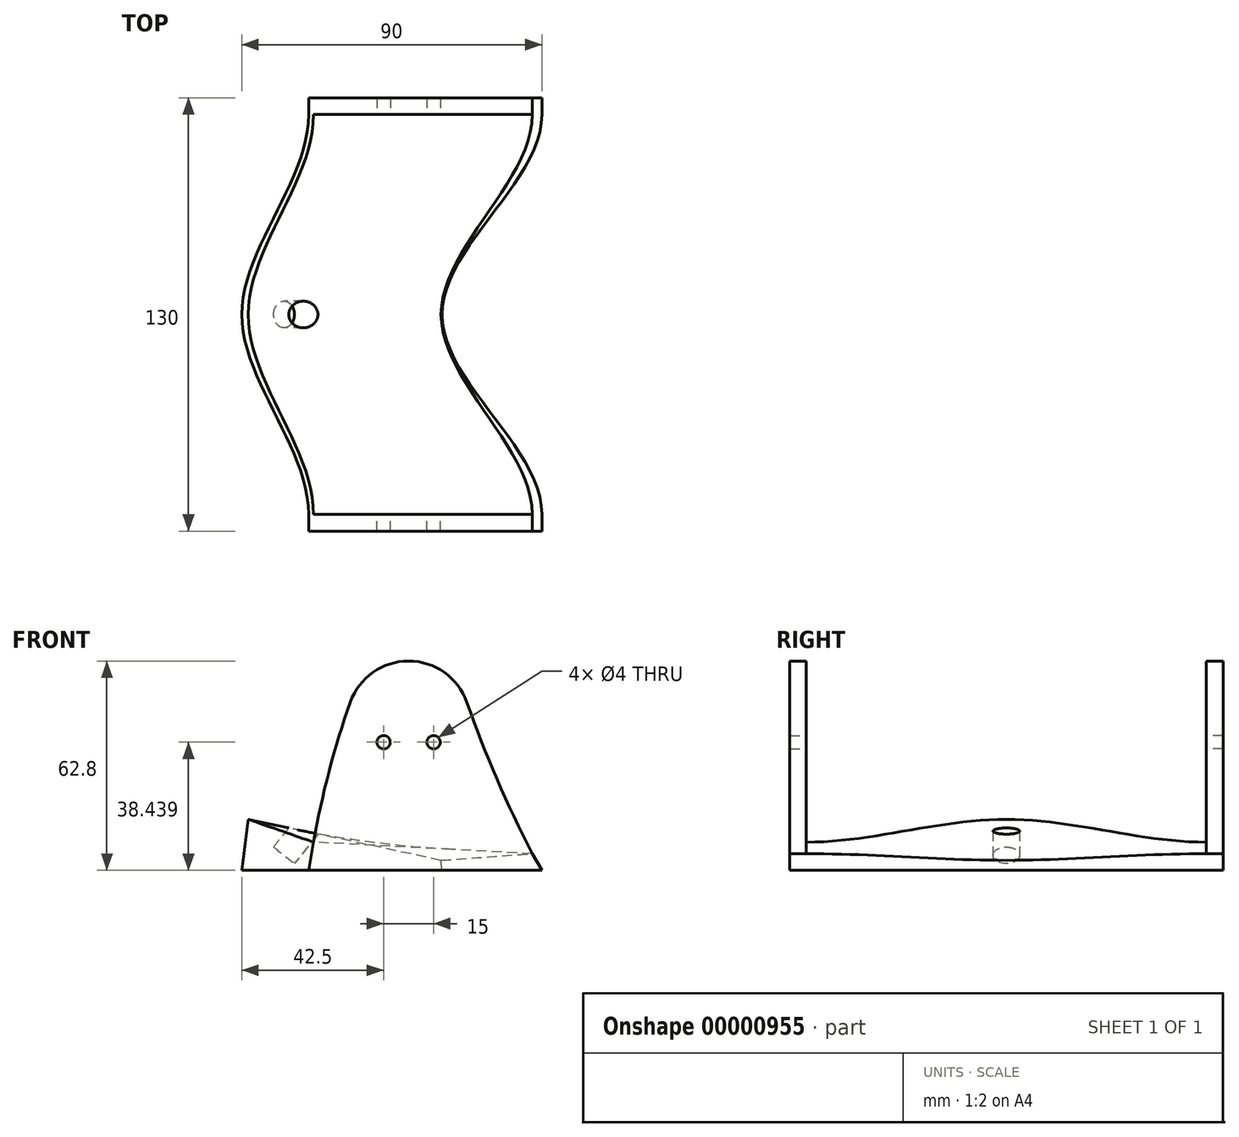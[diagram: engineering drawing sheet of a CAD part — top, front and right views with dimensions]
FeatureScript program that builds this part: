
annotation { "Feature Type Name" : "Feature", "Feature Type Description" : "" }
export const myFeature = defineFeature(function(context is Context, id is Id, definition is map)
    precondition{}
    {
        {
            var Q0;
            Q0=qCreatedBy(makeId("Front.planeOp"),FACE);
            cPlane(context, id + "F0", {"entities" : qUnion([Q0]), "cplaneType" : CPlaneType.OFFSET, "offset" : 60 * mm, "width" : 150 * mm, "height" : 150 * mm});
        }
        {
            var Q0;
            Q0=qCreatedBy(makeId("Front.planeOp"),FACE);
            var sketch = newSketch(context, id + "F1", { "sketchPlane" : qUnion([Q0])});
            skLineSegment(sketch, "E0", {"start": v(10, 0) * mm, "end": v(9.74, 3) * mm});
            skLineSegment(sketch, "E1", {"start": v(9.74, 3) * mm, "end": v(-48.12, 15.3) * mm});
            skLineSegment(sketch, "E2", {"start": v(-48.12, 15.3) * mm, "end": v(-50, 0) * mm});
            skLineSegment(sketch, "E3", {"start": v(-50, 0) * mm, "end": v(10, 0) * mm});
            skLineSegment(sketch, "E4", {"start": v(-50, 0) * mm, "end": v(-50, 45.23) * mm, "construction": true});
            skLineSegment(sketch, "E5", {"start": v(10, 0) * mm, "end": v(10, 34.67) * mm, "construction": true});
            skSolve(sketch);
        }
        {
            var Q0;
            Q0=qCreatedBy(id+"F0.planeOp",FACE);
            var sketch = newSketch(context, id + "F2", { "sketchPlane" : qUnion([Q0])});
            skLineSegment(sketch, "E6", {"start": v(40, 0) * mm, "end": v(37.11, 5) * mm});
            skLineSegment(sketch, "E7", {"start": v(37.11, 5) * mm, "end": v(-28.51, 8.44) * mm});
            skLineSegment(sketch, "E8", {"start": v(-28.51, 8.44) * mm, "end": v(-30, 0) * mm});
            skLineSegment(sketch, "E9", {"start": v(-30, 0) * mm, "end": v(40, 0) * mm});
            skLineSegment(sketch, "E10", {"start": v(-30, 0) * mm, "end": v(-30, 20.3) * mm, "construction": true});
            skLineSegment(sketch, "E11", {"start": v(40, 0) * mm, "end": v(40, 19.73) * mm, "construction": true});
            skSolve(sketch);
        }
        {
            var Q0;
            Q0=makeQuery(id+"F1.imprint","IMPRINT",FACE,{"disambiguationData":[TD([[makeQuery(id+"F1.imprint","IMPRINT",EDGE,{"derivedFrom":sQuery(id+"F1.wireOp",EDGE,"E0")}),1.0]])]});
            var Q1;
            Q1=makeQuery(id+"F2.imprint","IMPRINT",FACE,{"disambiguationData":[TD([[makeQuery(id+"F2.imprint","IMPRINT",EDGE,{"derivedFrom":sQuery(id+"F2.wireOp",EDGE,"E6")}),1.0]])]});
            loft(context, id + "F3", {"startCondition" : LoftEndDerivativeType.NORMAL_TO_PROFILE, "startMagnitude" : 1, "endCondition" : LoftEndDerivativeType.NORMAL_TO_PROFILE, "endMagnitude" : 1, "sheetProfilesArray" : [{ "sheetProfileEntities" : qUnion([Q0]) }, { "sheetProfileEntities" : qUnion([Q1]) }]});
        }
        {
            var Q0;
            Q0=qCreatedBy(id+"F0.planeOp",FACE);
            var sketch = newSketch(context, id + "F4", { "sketchPlane" : qUnion([Q0])});
            skLineSegment(sketch, "E12.0.0", {"start": v(-28.51, 8.44) * mm, "end": v(-30, 0) * mm});
            skLineSegment(sketch, "E12.0.1", {"start": v(-30, 0) * mm, "end": v(40, 0) * mm});
            skLineSegment(sketch, "E12.0.2", {"start": v(40, 0) * mm, "end": v(37.11, 5) * mm});
            skLineSegment(sketch, "E12.0.3", {"start": v(37.11, 5) * mm, "end": v(-28.51, 8.44) * mm, "construction": true});
            skLineSegment(sketch, "E13", {"start": v(-28.51, 8.44) * mm, "end": v(-17.47, 50.44) * mm, "construction": true});
            skLineSegment(sketch, "E14", {"start": v(-17.47, 50.44) * mm, "end": v(17.47, 50.44) * mm, "construction": true});
            skArc(sketch, "E15", {"start": v(-17.47, 50.44) * mm, "mid": v(-23.86, 29.67) * mm, "end": v(-28.51, 8.44) * mm});
            skArc(sketch, "E16", {"start": v(17.47, 50.44) * mm, "mid": v(0, 62.8) * mm, "end": v(-17.47, 50.44) * mm});
            skArc(sketch, "E17", {"start": v(17.47, 50.44) * mm, "mid": v(26.51, 27.38) * mm, "end": v(37.11, 5) * mm});
            skCircle(sketch, "E18", {"center": v(0, 48.44) * mm, "radius": 2.5 * mm, "construction": true});
            skCircle(sketch, "E19", {"center": v(7.5, 38.44) * mm, "radius": 2 * mm});
            skCircle(sketch, "E20", {"center": v(-7.5, 38.44) * mm, "radius": 2 * mm});
            skLineSegment(sketch, "E21", {"start": v(0, 48.44) * mm, "end": v(-7.5, 38.44) * mm, "construction": true});
            skLineSegment(sketch, "E22", {"start": v(-7.5, 38.44) * mm, "end": v(7.5, 38.44) * mm, "construction": true});
            skLineSegment(sketch, "E23", {"start": v(7.5, 38.44) * mm, "end": v(0, 48.44) * mm, "construction": true});
            skCircle(sketch, "E24", {"center": v(-7.5, 38.44) * mm, "radius": 5 * mm, "construction": true});
            skCircle(sketch, "E25", {"center": v(7.5, 38.44) * mm, "radius": 5 * mm, "construction": true});
            skCircle(sketch, "E26", {"center": v(0, 48.44) * mm, "radius": 5 * mm, "construction": true});
            skSolve(sketch);
        }
        {
            var Q0;
            Q0 = qSketchRegion(id + "F4", true);
            extrude(context, id + "F5", {"entities" : qUnion([Q0]), "operationType" : NewBodyOperationType.ADD, "depth" : 5 * mm, "offsetDistance" : 25 * mm});
        }
        {
            var Q0;
            Q0=makeQuery(id+"F3.opLoft","CAP_FACE",FACE,{"disambiguationData":[OSD([makeQuery(id+"F1.imprint","IMPRINT",FACE,{"disambiguationData":[TD([[makeQuery(id+"F1.imprint","IMPRINT",EDGE,{"derivedFrom":sQuery(id+"F1.wireOp",EDGE,"E0")}),1.0]])]})])],"isStart":true});
            var sketch = newSketch(context, id + "F6", { "sketchPlane" : qUnion([Q0])});
            skArc(sketch, "E27.0", {"start": v(-17.47, 50.44) * mm, "mid": v(0, 62.8) * mm, "end": v(17.47, 50.44) * mm, "construction": true});
            skLineSegment(sketch, "E28.0", {"start": v(-9.74, 3) * mm, "end": v(48.12, 15.3) * mm, "construction": true});
            skLineSegment(sketch, "E29", {"start": v(0, 51.44) * mm, "end": v(24.9, 20.14) * mm, "construction": true});
            skLineSegment(sketch, "E30", {"start": v(0, 51.44) * mm, "end": v(37.7, 51.44) * mm, "construction": true});
            skCircle(sketch, "E31", {"center": v(0, 51.44) * mm, "radius": 40 * mm, "construction": true});
            skLineSegment(sketch, "E32", {"start": v(24.9, 20.14) * mm, "end": v(37.36, 4.5) * mm, "construction": true});
            skLineSegment(sketch, "E33", {"start": v(37.36, 4.5) * mm, "end": v(34.23, 2) * mm});
            skLineSegment(sketch, "E34", {"start": v(21.78, 17.65) * mm, "end": v(24.9, 20.14) * mm});
            skLineSegment(sketch, "E35", {"start": v(21.78, 17.65) * mm, "end": v(34.23, 2) * mm});
            skLineSegment(sketch, "E36", {"start": v(24.9, 20.14) * mm, "end": v(37.36, 4.5) * mm});
            skSolve(sketch);
        }
        {
            var Q0;
            Q0 = qSketchRegion(id + "F6", true);
            var Q1;
            Q1=sQuery(id+"F6.wireOp",EDGE,"E29");
            revolve(context, id + "F7", {"operationType" : NewBodyOperationType.REMOVE, "surfaceOperationType" : NewSurfaceOperationType.NEW, "entities" : qUnion([Q0]), "axis" : qUnion([Q1]), "revolveType" : RevolveType.FULL, "oppositeDirection" : true});
        }
        {
            var Q0;
            Q0=makeQuery(id+"F3.opLoft","SWEPT_BODY",BODY,{"disambiguationData":[OSD([makeQuery(id+"F1.imprint","IMPRINT",FACE,{"disambiguationData":[TD([[makeQuery(id+"F1.imprint","IMPRINT",EDGE,{"derivedFrom":sQuery(id+"F1.wireOp",EDGE,"E0")}),1.0]])]}),makeQuery(id+"F2.imprint","IMPRINT",FACE,{"disambiguationData":[TD([[makeQuery(id+"F2.imprint","IMPRINT",EDGE,{"derivedFrom":sQuery(id+"F2.wireOp",EDGE,"E6")}),1.0]])]})])]});
            var Q1;
            Q1=makeQuery(id+"F3.opLoft","CAP_FACE",FACE,{"disambiguationData":[OSD([makeQuery(id+"F1.imprint","IMPRINT",FACE,{"disambiguationData":[TD([[makeQuery(id+"F1.imprint","IMPRINT",EDGE,{"derivedFrom":sQuery(id+"F1.wireOp",EDGE,"E0")}),1.0]])]})])],"isStart":true});
            mirror(context, id + "F8", {"operationType" : NewBodyOperationType.ADD, "entities" : qUnion([Q0]), "mirrorPlane" : qUnion([Q1])});
        }
    });
